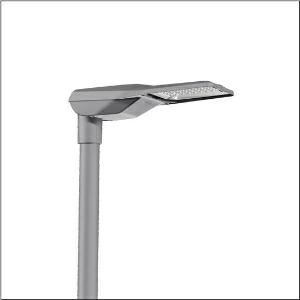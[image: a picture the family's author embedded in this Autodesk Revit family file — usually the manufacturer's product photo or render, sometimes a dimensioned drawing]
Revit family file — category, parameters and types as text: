
# Revit family: streetlight_sl_21_mini___st1_0a_5xe6d33a08hb_3337
name_source: partatom
category: Lighting Fixtures
units: mm (PartAtom-declared; Revit-internal decimal feet)

## family parameters
Cut with Voids When Loaded = No
Host = Face
Light Source = No
Part Type = Normal
Room Calculation Point = No
Round Connector Dimension = Use Diameter
Shared = No

## types (1)
- --- (1 x LED, 9040 lm, 66 W, 3000K)
    Apparent Load = 66 VA
    CIE Flux Codes = 37 72 97 100 100
    Color Rendering = 70
    Color Temperature = 3000K
    Default Elevation = 1800 mm
    Description = Streetlight SL 21 mini, mast luminaire, primary light control with lens, of PMMA, primary optical cover: cover, of toughened safety glass, transparent, light distribution: ST1.0a, light emission: direct distribution, primary light characteristic: asymmetric, installation type: post-top, side-entry, LED, 3G 1.5mm², High Power LED, rated luminous flux: 9.040lm, luminous efficacy: 137lm/W, light colour: 730, colour temperature: 3000K, control: flexible luminous flux parameterisation, time-dependent luminous flux control, constant luminous flux control, overheat protection, mains connection: 230..240V, AC, 50/60Hz, connection cable pre-assembled, cable length: 8,5m, wiring characteristics: H07RN-F, start of lifetime: 66W, end of service life: 69W, reduction: 30W, luminaire housing, of diecast aluminium, powder-coated, Siteco® metallic grey (DB 702S), corrosivity category C5 mid according to DIN EN ISO 12944, please order mast flange separately, inclination adjustable: 0°, 5°, 10°, 15°, sealing non-destructively replaceable, multi-level sealing system, length: 628mm, width: 235mm, height: 110mm, mast flange for spigot size: 42mm (side-entry): 5XC10008XM4, 60/48mm (side-entry/post-top): 5XC10108XM2, 76/60mm (side-entry/post-top): 5XC10108XM1, protection rating (complete): IP66, insulation class (complete): insulation class II (safety insulation), certification: CE, ENEC, ENEC+, VDE, impact resistance: IK09, permissible operating ambient temperature for outdoor applications: -40..+50°C, standard-compliant lighting for roads and squares, packaging unit: 1 piece

Light Distribution: ST1.0a
    Height = 110 mm
    Lamp = 1 x LED
    Lamp Light Flux = 9040 lm
    Lamp Power = 66 W
    Lamp count = 1
    Length = 625 mm
    Luminous efficacy = 137 lm/W
    Manufacturer = Siteco
    ModVariant = No
    Model = 5XE6D33A08HB
    Number of Poles = 1
    OnlyDefault = Yes
    Power Factor = 1
    Product Name = Streetlight SL 21 mini | ST1.0a
    Product group = mast luminaire | pylon top
    ProductGroupID = 6100
    Protection Class = Protection class II
    Protection Degree = IP 66
    RLX_Detail_Level = 1
    RLX_Emergency_Light_Flux = 0 lm
    RLX_Emergency_Type = 0
    RLX_Emergency_Type_DB = No
    RlxData = <blob elided: 91949 chars, md5=141b13bc>
    Socket = socket
    Standby Power = 0 W
    System Light Flux = 9040 lm
    System Power = 66 W
    Type Comments = factory setting: luminous flux: 100 % | Output Level: 100 % | 670 mA
    Type Image = l_1003519.jpg
    URL = http://relux.com
    VarID = @adj_121977
    Voltage = 0 V
    Weight = 0.00 kg
    Width = 234 mm

## geometry (parser evidence)
native form markers: Blend x4, Sweep x11
no freeform markers — native parametric forms only
